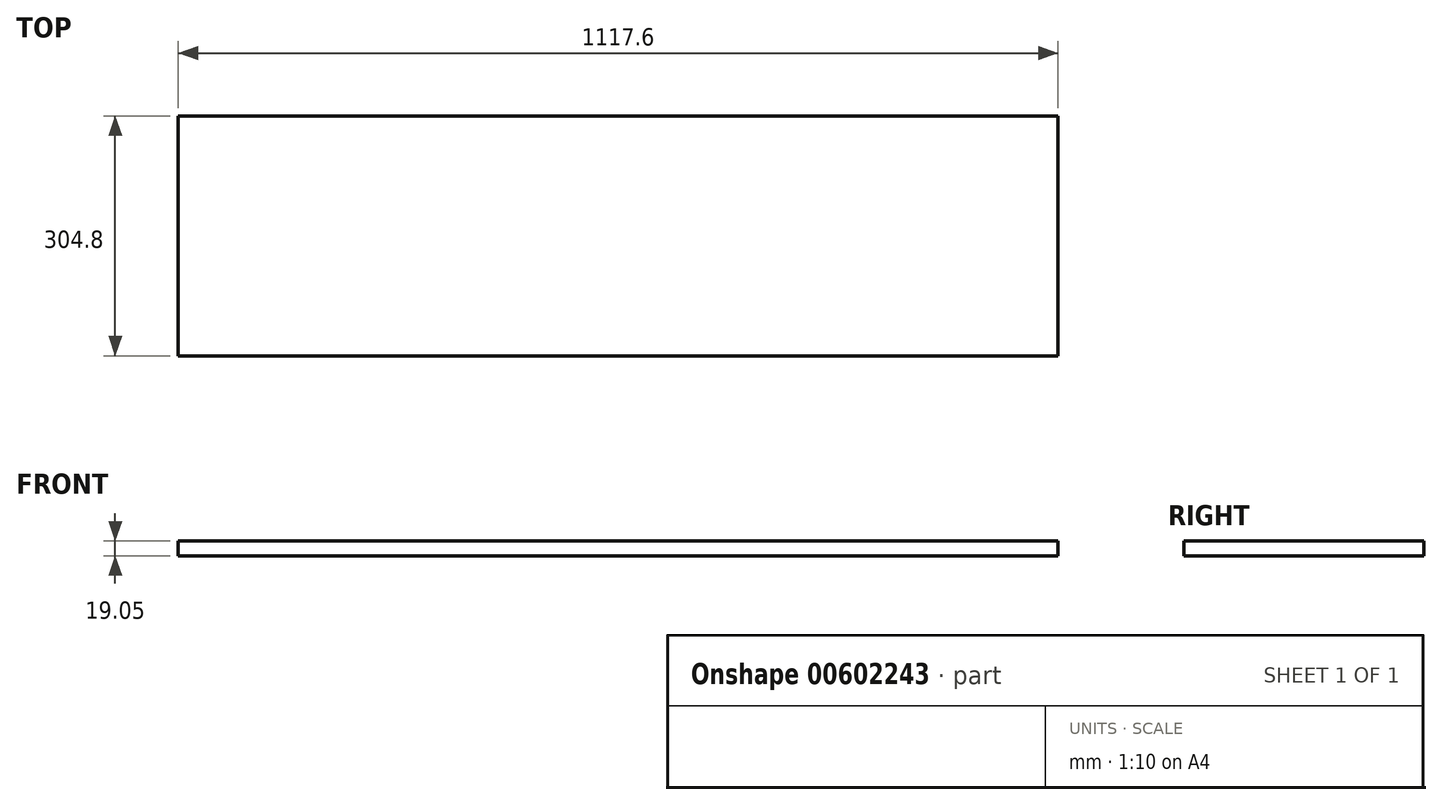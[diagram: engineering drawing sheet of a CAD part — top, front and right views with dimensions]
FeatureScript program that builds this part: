
annotation { "Feature Type Name" : "Feature", "Feature Type Description" : "" }
export const myFeature = defineFeature(function(context is Context, id is Id, definition is map)
    precondition{}
    {
        {
            var Q0;
            Q0=qCreatedBy(makeId("Top.planeOp"),FACE);
            var sketch = newSketch(context, id + "F0", { "sketchPlane" : qUnion([Q0])});
            skLineSegment(sketch, "E0.bottom", {"start": v(681.19, -135.23) * mm, "end": v(-436.41, -135.23) * mm});
            skLineSegment(sketch, "E0.top", {"start": v(681.19, 169.57) * mm, "end": v(-436.41, 169.57) * mm});
            skLineSegment(sketch, "E0.left", {"start": v(681.19, -135.23) * mm, "end": v(681.19, 169.57) * mm});
            skLineSegment(sketch, "E0.right", {"start": v(-436.41, -135.23) * mm, "end": v(-436.41, 169.57) * mm});
            skPoint(sketch, "E0.middle", {"position": v(122.39, 17.17) * mm});
            skSolve(sketch);
        }
        {
            var Q0;
            Q0=makeQuery(id+"F0.imprint","IMPRINT",FACE,{"disambiguationData":[TD([[makeQuery(id+"F0.imprint","IMPRINT",EDGE,{"derivedFrom":sQuery(id+"F0.wireOp",EDGE,"E0.bottom")}),-1.0]])]});
            extrude(context, id + "F1", {"entities" : qUnion([Q0]), "depth" : 19.05 * mm, "offsetDistance" : 25.4 * mm});
        }
    });
